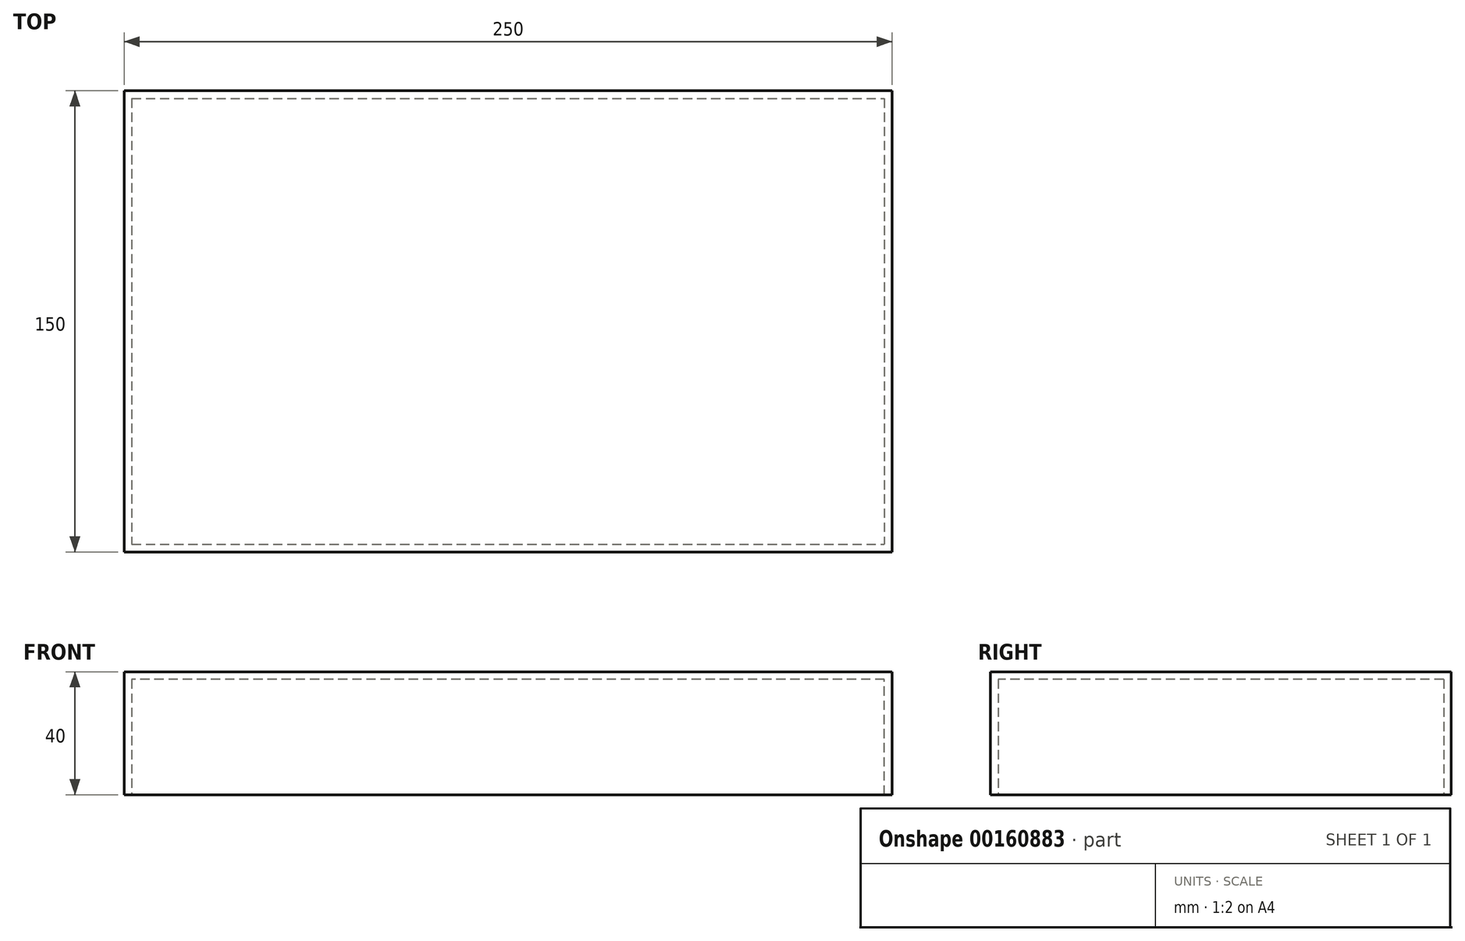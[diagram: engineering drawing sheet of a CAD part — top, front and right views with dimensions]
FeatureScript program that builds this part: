
annotation { "Feature Type Name" : "Feature", "Feature Type Description" : "" }
export const myFeature = defineFeature(function(context is Context, id is Id, definition is map)
    precondition{}
    {
        {
            var Q0;
            Q0=qCreatedBy(makeId("Front.planeOp"),FACE);
            var sketch = newSketch(context, id + "F0", { "sketchPlane" : qUnion([Q0])});
            skLineSegment(sketch, "E0", {"start": v(-250, 40) * mm, "end": v(-250, 0) * mm});
            skLineSegment(sketch, "E1", {"start": v(-250, 0) * mm, "end": v(0, 0) * mm});
            skLineSegment(sketch, "E2", {"start": v(0, 0) * mm, "end": v(0, 40) * mm});
            skLineSegment(sketch, "E3", {"start": v(0, 40) * mm, "end": v(-250, 40) * mm});
            skSolve(sketch);
        }
        {
            var Q0;
            Q0=makeQuery(id+"F0.imprint","IMPRINT",FACE,{"disambiguationData":[TD([[makeQuery(id+"F0.imprint","IMPRINT",EDGE,{"derivedFrom":sQuery(id+"F0.wireOp",EDGE,"E0")}),1.0]])]});
            extrude(context, id + "F1", {"entities" : qUnion([Q0]), "oppositeDirection" : true, "depth" : 150 * mm});
        }
        {
            var Q0;
            Q0=makeQuery(id+"F1.opExtrude","SWEPT_FACE",FACE,{"disambiguationData":[OSD([sQuery(id+"F0.wireOp",EDGE,"E1")])]});
            shell(context, id + "F2", {"entities" : qUnion([Q0]), "thickness" : 2.5 * mm});
        }
        {
            var Q0;
            Q0=qCreatedBy(makeId("Front.planeOp"),FACE);
            var sketch = newSketch(context, id + "F3", { "sketchPlane" : qUnion([Q0])});
            skLineSegment(sketch, "E4", {"start": v(0, 0) * mm, "end": v(10, 0) * mm});
            skLineSegment(sketch, "E5", {"start": v(10, 2.5) * mm, "end": v(0, 2.5) * mm});
            skLineSegment(sketch, "E6", {"start": v(10, 2.5) * mm, "end": v(10, 0) * mm});
            skSolve(sketch);
        }
        {
            var Q0;
            Q0=sQuery(id+"F3.wireOp",EDGE,"E4");
            var Q1;
            Q1=sQuery(id+"F3.wireOp",EDGE,"E5");
            var Q2;
            Q2=sQuery(id+"F3.wireOp",EDGE,"E6");
            extrude(context, id + "F4", {"bodyType" : ToolBodyType.SURFACE, "surfaceEntities" : qUnion([Q0, Q1, Q2]), "oppositeDirection" : true, "depth" : 150 * mm});
        }
        {
            var Q0;
            Q0=makeQuery(id+"F1.opExtrude","CAP_FACE",FACE,{"disambiguationData":[OSD([sQuery(id+"F0.wireOp",EDGE,"E0"),sQuery(id+"F0.wireOp",EDGE,"E1"),sQuery(id+"F0.wireOp",EDGE,"E2"),sQuery(id+"F0.wireOp",EDGE,"E3")])],"isStart":false});
            var sketch = newSketch(context, id + "F5", { "sketchPlane" : qUnion([Q0])});
            skLineSegment(sketch, "E7", {"start": v(250, 0) * mm, "end": v(260, 0) * mm});
            skLineSegment(sketch, "E8", {"start": v(260, 0) * mm, "end": v(260, 2.5) * mm});
            skLineSegment(sketch, "E9", {"start": v(260, 2.5) * mm, "end": v(250, 2.5) * mm});
            skSolve(sketch);
        }
        {
            var Q0;
            Q0=sQuery(id+"F5.wireOp",EDGE,"E9");
            var Q1;
            Q1=sQuery(id+"F5.wireOp",EDGE,"E7");
            var Q2;
            Q2=sQuery(id+"F5.wireOp",EDGE,"E8");
            extrude(context, id + "F6", {"bodyType" : ToolBodyType.SURFACE, "surfaceEntities" : qUnion([Q0, Q1, Q2]), "oppositeDirection" : true, "depth" : 150 * mm});
        }
        {
            var Q0;
            Q0=qCreatedBy(makeId("Front.planeOp"),FACE);
            var sketch = newSketch(context, id + "F7", { "sketchPlane" : qUnion([Q0])});
            skLineSegment(sketch, "E10", {"start": v(0, -5) * mm, "end": v(-250, -5) * mm});
            skLineSegment(sketch, "E11", {"start": v(0, -5) * mm, "end": v(10, -5) * mm});
            skLineSegment(sketch, "E12", {"start": v(-250, -5) * mm, "end": v(-260, -5) * mm});
            skLineSegment(sketch, "E13", {"start": v(-260, -5) * mm, "end": v(-260, 0) * mm});
            skLineSegment(sketch, "E14", {"start": v(10, -5) * mm, "end": v(10, 0) * mm});
            skLineSegment(sketch, "E15", {"start": v(-260, 0) * mm, "end": v(10, 0) * mm});
            skSolve(sketch);
        }
        {
            var Q0;
            Q0=sQuery(id+"F7.wireOp",EDGE,"E13");
            var Q1;
            Q1=sQuery(id+"F7.wireOp",EDGE,"E12");
            var Q2;
            Q2=sQuery(id+"F7.wireOp",EDGE,"E10");
            var Q3;
            Q3=sQuery(id+"F7.wireOp",EDGE,"E11");
            var Q4;
            Q4=sQuery(id+"F7.wireOp",EDGE,"E14");
            var Q5;
            Q5=sQuery(id+"F7.wireOp",EDGE,"E15");
            extrude(context, id + "F8", {"bodyType" : ToolBodyType.SURFACE, "surfaceEntities" : qUnion([Q0, Q1, Q2, Q3, Q4, Q5]), "oppositeDirection" : true, "depth" : 150 * mm});
        }
        {
            var Q0;
            Q0=makeQuery(id+"F8.opExtrude","SWEPT_BODY",BODY,{"disambiguationData":[OSD([sQuery(id+"F7.wireOp",EDGE,"E10"),sQuery(id+"F7.wireOp",EDGE,"E11"),sQuery(id+"F7.wireOp",EDGE,"E12")])]});
            var Q1;
            Q1=makeQuery(id+"F8.opExtrude","SWEPT_FACE",FACE,{"disambiguationData":[OSD([sQuery(id+"F7.wireOp",EDGE,"E10"),sQuery(id+"F7.wireOp",EDGE,"E11"),sQuery(id+"F7.wireOp",EDGE,"E12")])]});
            transform(context, id + "F9", {"entities" : qUnion([Q0]), "transformType" : TransformType.TRANSLATION_DISTANCE, "transformDirection" : qUnion([Q1]), "distance" : 10 * mm, "makeCopy" : false});
        }
    });
